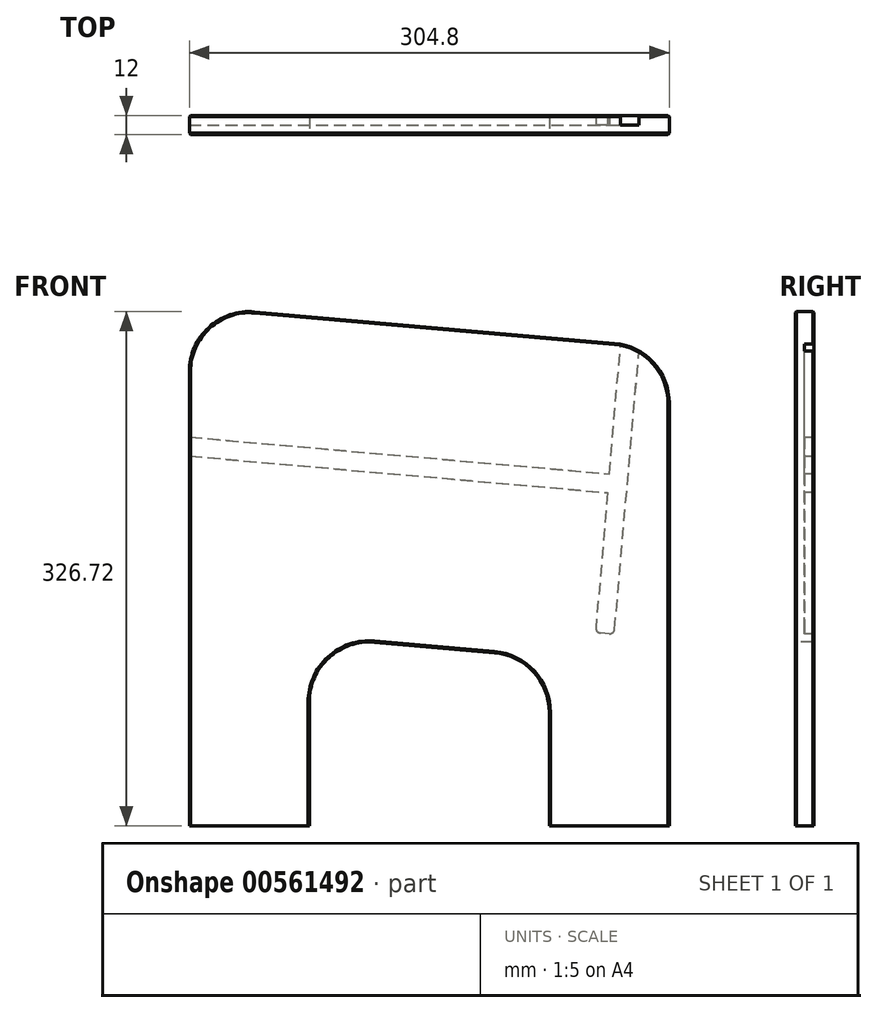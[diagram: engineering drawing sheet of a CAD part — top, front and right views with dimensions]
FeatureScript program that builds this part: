
annotation { "Feature Type Name" : "Feature", "Feature Type Description" : "" }
export const myFeature = defineFeature(function(context is Context, id is Id, definition is map)
    precondition{}
    {
        {
            var Q0;
            Q0=qCreatedBy(makeId("Front.planeOp"),FACE);
            var sketch = newSketch(context, id + "F0", { "sketchPlane" : qUnion([Q0])});
            skLineSegment(sketch, "E0", {"start": v(-76.2, 0) * mm, "end": v(-152.4, 0) * mm});
            skLineSegment(sketch, "E1", {"start": v(-152.4, 0) * mm, "end": v(-152.4, 288.62) * mm});
            skLineSegment(sketch, "E2", {"start": v(-110.98, 326.58) * mm, "end": v(117.62, 306.58) * mm});
            skLineSegment(sketch, "E3", {"start": v(152.4, 268.62) * mm, "end": v(152.4, 0) * mm});
            skLineSegment(sketch, "E4", {"start": v(152.4, 0) * mm, "end": v(76.2, 0) * mm});
            skLineSegment(sketch, "E5", {"start": v(76.2, 0) * mm, "end": v(76.2, 72.09) * mm});
            skLineSegment(sketch, "E6", {"start": v(41.42, 110.04) * mm, "end": v(-34.78, 116.7) * mm});
            skLineSegment(sketch, "E7", {"start": v(-76.2, 78.75) * mm, "end": v(-76.2, 0) * mm});
            skLineSegment(sketch, "E8", {"start": v(-76.2, 0) * mm, "end": v(76.2, 0) * mm, "construction": true});
            skPoint(sketch, "E9.visualSharp", {"position": v(-152.4, 330.2) * mm});
            skArc(sketch, "E9.filletArc", {"start": v(-110.98, 326.58) * mm, "mid": v(-140.04, 316.71) * mm, "end": v(-152.4, 288.62) * mm});
            skPoint(sketch, "E10.visualSharp", {"position": v(152.4, 303.53) * mm});
            skArc(sketch, "E10.filletArc", {"start": v(152.4, 268.62) * mm, "mid": v(142.4, 294.36) * mm, "end": v(117.62, 306.58) * mm});
            skPoint(sketch, "E11.visualSharp", {"position": v(-76.2, 120.33) * mm});
            skArc(sketch, "E11.filletArc", {"start": v(-34.78, 116.7) * mm, "mid": v(-63.84, 106.84) * mm, "end": v(-76.2, 78.75) * mm});
            skPoint(sketch, "E12.visualSharp", {"position": v(76.2, 107) * mm});
            skArc(sketch, "E12.filletArc", {"start": v(76.2, 72.09) * mm, "mid": v(66.2, 97.83) * mm, "end": v(41.42, 110.04) * mm});
            skLineSegment(sketch, "E13", {"start": v(-34.78, 116.7) * mm, "end": v(-152.4, 127) * mm, "construction": true});
            skLineSegment(sketch, "E14", {"start": v(-76.2, 0) * mm, "end": v(-76.2, 197.84) * mm, "construction": true});
            skLineSegment(sketch, "E15", {"start": v(-110.98, 326.58) * mm, "end": v(-262.29, 339.81) * mm, "construction": true});
            skLineSegment(sketch, "E16", {"start": v(-152.4, 0) * mm, "end": v(-152.4, 497.67) * mm, "construction": true});
            skSolve(sketch);
        }
        {
            var Q0;
            Q0 = qSketchRegion(id + "F0", true);
            extrude(context, id + "F1", {"entities" : qUnion([Q0]), "oppositeDirection" : true, "depth" : 12 * mm, "offsetDistance" : 25.4 * mm, "symmetric" : true});
        }
        {
            var Q0;
            Q0=qCreatedBy(makeId("Front.planeOp"),FACE);
            var sketch = newSketch(context, id + "F2", { "sketchPlane" : qUnion([Q0])});
            skLineSegment(sketch, "E17", {"start": v(-152.4, 247) * mm, "end": v(114.33, 223.66) * mm});
            skLineSegment(sketch, "E18", {"start": v(114.33, 223.66) * mm, "end": v(121.87, 309.82) * mm});
            skLineSegment(sketch, "E19", {"start": v(121.87, 309.82) * mm, "end": v(133.82, 308.78) * mm});
            skLineSegment(sketch, "E20", {"start": v(133.82, 308.78) * mm, "end": v(117.99, 127.75) * mm});
            skLineSegment(sketch, "E21", {"start": v(-152.4, 247) * mm, "end": v(-152.4, 234.95) * mm, "construction": true});
            skLineSegment(sketch, "E22", {"start": v(-152.4, 234.95) * mm, "end": v(113.29, 211.7) * mm});
            skLineSegment(sketch, "E23", {"start": v(113.29, 211.7) * mm, "end": v(106.03, 128.8) * mm});
            skArc(sketch, "E24", {"start": v(106.03, 128.8) * mm, "mid": v(111.49, 122.3) * mm, "end": v(117.99, 127.75) * mm, "construction": true});
            skLineSegment(sketch, "E25", {"start": v(-152.4, 240.97) * mm, "end": v(219.15, 208.47) * mm, "construction": true});
            skLineSegment(sketch, "E26", {"start": v(-152.4, 247) * mm, "end": v(-156.2, 247.33) * mm});
            skLineSegment(sketch, "E27", {"start": v(-156.2, 247.33) * mm, "end": v(-157.24, 235.37) * mm});
            skLineSegment(sketch, "E28", {"start": v(-157.24, 235.37) * mm, "end": v(-152.4, 234.95) * mm});
            skPoint(sketch, "E29", {"position": v(121.54, 306.03) * mm});
            skLineSegment(sketch, "E30", {"start": v(114.3, 122.05) * mm, "end": v(108.67, 122.54) * mm});
            skLineSegment(sketch, "E31", {"start": v(117.74, 124.93) * mm, "end": v(117.99, 127.75) * mm});
            skLineSegment(sketch, "E32", {"start": v(105.78, 125.98) * mm, "end": v(106.03, 128.8) * mm});
            skPoint(sketch, "E33.0.visualSharp", {"position": v(117.46, 121.77) * mm});
            skArc(sketch, "E33.0.filletArc", {"start": v(114.3, 122.05) * mm, "mid": v(116.62, 122.78) * mm, "end": v(117.74, 124.93) * mm});
            skPoint(sketch, "E34.0.visualSharp", {"position": v(105.5, 122.82) * mm});
            skArc(sketch, "E34.0.filletArc", {"start": v(105.78, 125.98) * mm, "mid": v(106.52, 123.66) * mm, "end": v(108.67, 122.54) * mm});
            skSolve(sketch);
        }
        {
            var Q0;
            Q0 = qSketchRegion(id + "F2", true);
            extrude(context, id + "F3", {"entities" : qUnion([Q0]), "operationType" : NewBodyOperationType.REMOVE, "oppositeDirection" : true, "depth" : 6.35 * mm, "offsetDistance" : 25.4 * mm});
        }
        {
            var Q0;
            Q0=makeQuery(id+"F1.opExtrude","CAP_EDGE",EDGE,{"disambiguationData":[OSD([sQuery(id+"F0.wireOp",EDGE,"E2")])],"isStart":false});
            var Q1;
            {var subQ0=sQuery(id+"F0.wireOp",EDGE,"E10.filletArc");var subQ1=sQuery(id+"F0.wireOp",EDGE,"E3");Q1=makeQuery(id+"F3.boolean.opBoolean","SPLIT",EDGE,{"disambiguationData":[TD([makeQuery(id+"F1.opExtrude","SWEPT_FACE",FACE,{"disambiguationData":[OSD([subQ1])]})])],"derivedFrom":makeQuery(id+"F1.opExtrude","CAP_EDGE",EDGE,{"disambiguationData":[OSD([subQ0])],"isStart":false})});}
            var Q2;
            {var subQ0=sQuery(id+"F0.wireOp",EDGE,"E0");var subQ1=sQuery(id+"F0.wireOp",EDGE,"E1");Q2=makeQuery(id+"F3.boolean.opBoolean","SPLIT",EDGE,{"disambiguationData":[TD([makeQuery(id+"F1.opExtrude","SWEPT_FACE",FACE,{"disambiguationData":[OSD([subQ0])]})])],"derivedFrom":makeQuery(id+"F1.opExtrude","CAP_EDGE",EDGE,{"disambiguationData":[OSD([subQ1])],"isStart":false})});}
            var Q3;
            Q3=makeQuery(id+"F1.opExtrude","CAP_EDGE",EDGE,{"disambiguationData":[OSD([sQuery(id+"F0.wireOp",EDGE,"E3")])],"isStart":true});
            var Q4;
            Q4=makeQuery(id+"F1.opExtrude","CAP_EDGE",EDGE,{"disambiguationData":[OSD([sQuery(id+"F0.wireOp",EDGE,"E6")])],"isStart":true});
            var Q5;
            Q5=makeQuery(id+"F1.opExtrude","CAP_EDGE",EDGE,{"disambiguationData":[OSD([sQuery(id+"F0.wireOp",EDGE,"E6")])],"isStart":false});
            chamfer(context, id + "F4", {"entities" : qUnion([Q0, Q1, Q2, Q3, Q4, Q5]), "width" : 0.76 * mm, "tangentPropagation" : true});
        }
    });
